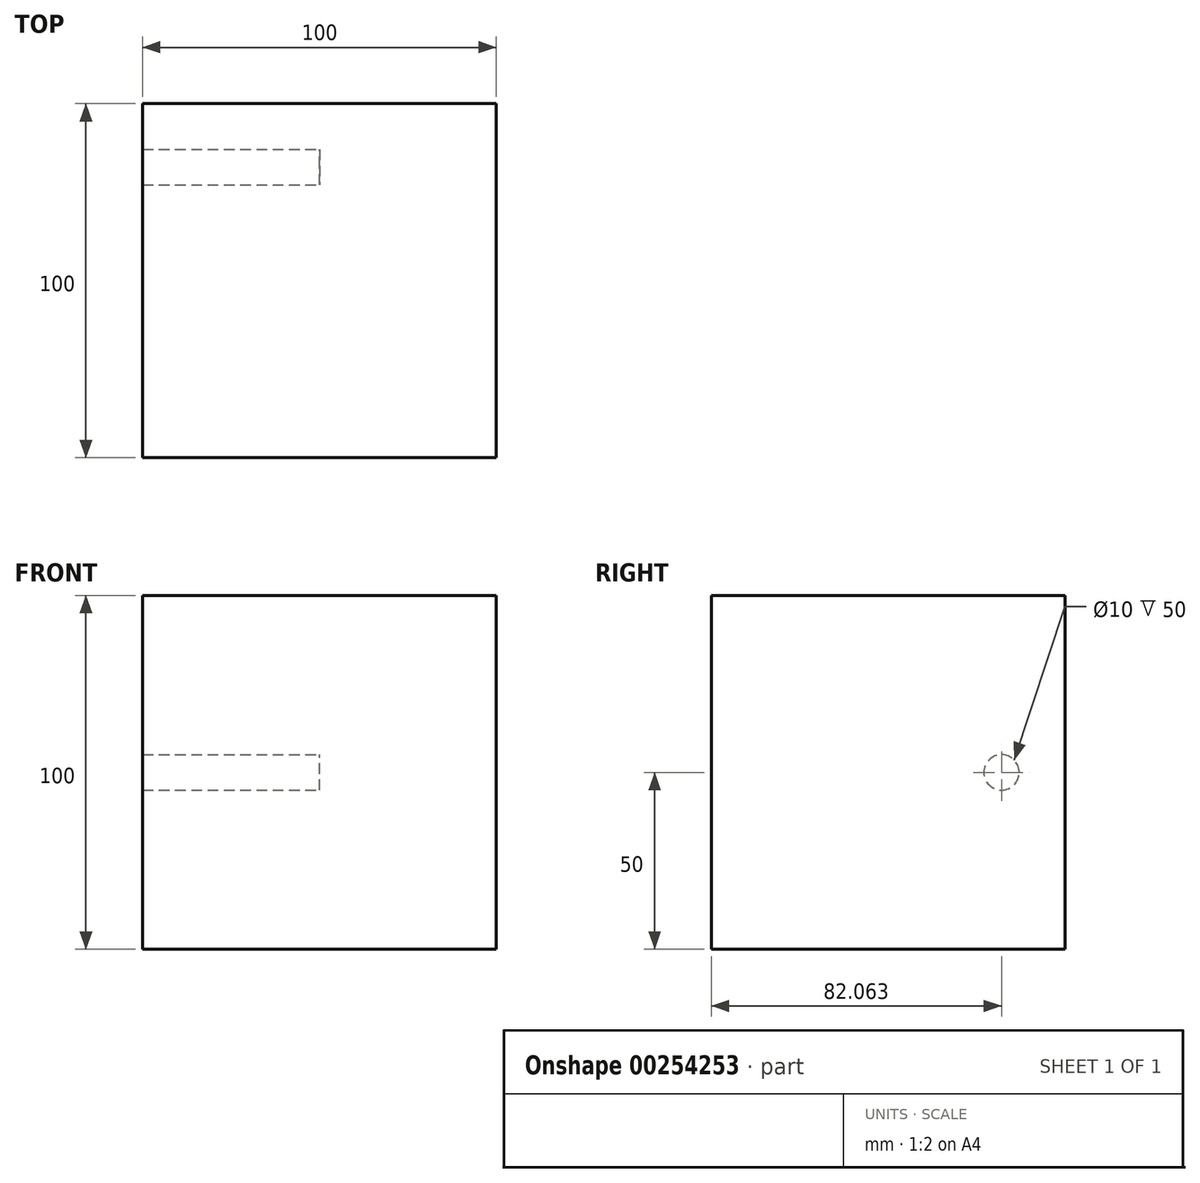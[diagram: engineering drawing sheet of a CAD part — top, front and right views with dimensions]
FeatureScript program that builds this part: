
annotation { "Feature Type Name" : "Feature", "Feature Type Description" : "" }
export const myFeature = defineFeature(function(context is Context, id is Id, definition is map)
    precondition{}
    {
        {
            var Q0;
            Q0=qCreatedBy(makeId("Front.planeOp"),FACE);
            var sketch = newSketch(context, id + "F0", { "sketchPlane" : qUnion([Q0])});
            skLineSegment(sketch, "E0.bottom", {"start": v(50, 50) * mm, "end": v(-50, 50) * mm});
            skLineSegment(sketch, "E0.top", {"start": v(50, -50) * mm, "end": v(-50, -50) * mm});
            skLineSegment(sketch, "E0.left", {"start": v(50, 50) * mm, "end": v(50, -50) * mm});
            skLineSegment(sketch, "E0.right", {"start": v(-50, 50) * mm, "end": v(-50, -50) * mm});
            skPoint(sketch, "E0.middle", {"position": v(0, 0) * mm});
            skSolve(sketch);
        }
        {
            var Q0;
            Q0=makeQuery(id+"F0.imprint","IMPRINT",FACE,{"disambiguationData":[TD([[makeQuery(id+"F0.imprint","IMPRINT",EDGE,{"derivedFrom":sQuery(id+"F0.wireOp",EDGE,"E0.bottom")}),1.0]])]});
            extrude(context, id + "F1", {"entities" : qUnion([Q0]), "depth" : 100 * mm});
        }
        {
            var Q0;
            Q0=qCreatedBy(makeId("Top.planeOp"),FACE);
            var sketch = newSketch(context, id + "F2", { "sketchPlane" : qUnion([Q0])});
            skCircle(sketch, "E1", {"center": v(0, -15.4) * mm, "radius": 5 * mm});
            skSolve(sketch);
        }
        {
            var Q0;
            Q0 = qSketchRegion(id + "F2", true);
            extrude(context, id + "F3", {"entities" : qUnion([Q0]), "operationType" : NewBodyOperationType.ADD, "depth" : 10 * mm});
        }
        {
            var Q0;
            Q0=qCreatedBy(makeId("Top.planeOp"),FACE);
            var sketch = newSketch(context, id + "F4", { "sketchPlane" : qUnion([Q0])});
            skCircle(sketch, "E2", {"center": v(0, -15.33) * mm, "radius": 5 * mm});
            skSolve(sketch);
        }
        {
            var Q0;
            Q0 = qSketchRegion(id + "F4", true);
            extrude(context, id + "F5", {"entities" : qUnion([Q0]), "operationType" : NewBodyOperationType.ADD, "depth" : 10 * mm});
        }
        {
            var Q0;
            Q0=qCreatedBy(makeId("Right.planeOp"),FACE);
            var sketch = newSketch(context, id + "F6", { "sketchPlane" : qUnion([Q0])});
            skCircle(sketch, "E3", {"center": v(-17.94, 0) * mm, "radius": 5 * mm});
            skSolve(sketch);
        }
        {
            var Q0;
            Q0 = qSketchRegion(id + "F6", true);
            extrude(context, id + "F7", {"entities" : qUnion([Q0]), "operationType" : NewBodyOperationType.REMOVE, "endBound" : BoundingType.THROUGH_ALL, "oppositeDirection" : true, "depth" : 5000 * mm});
        }
    });
